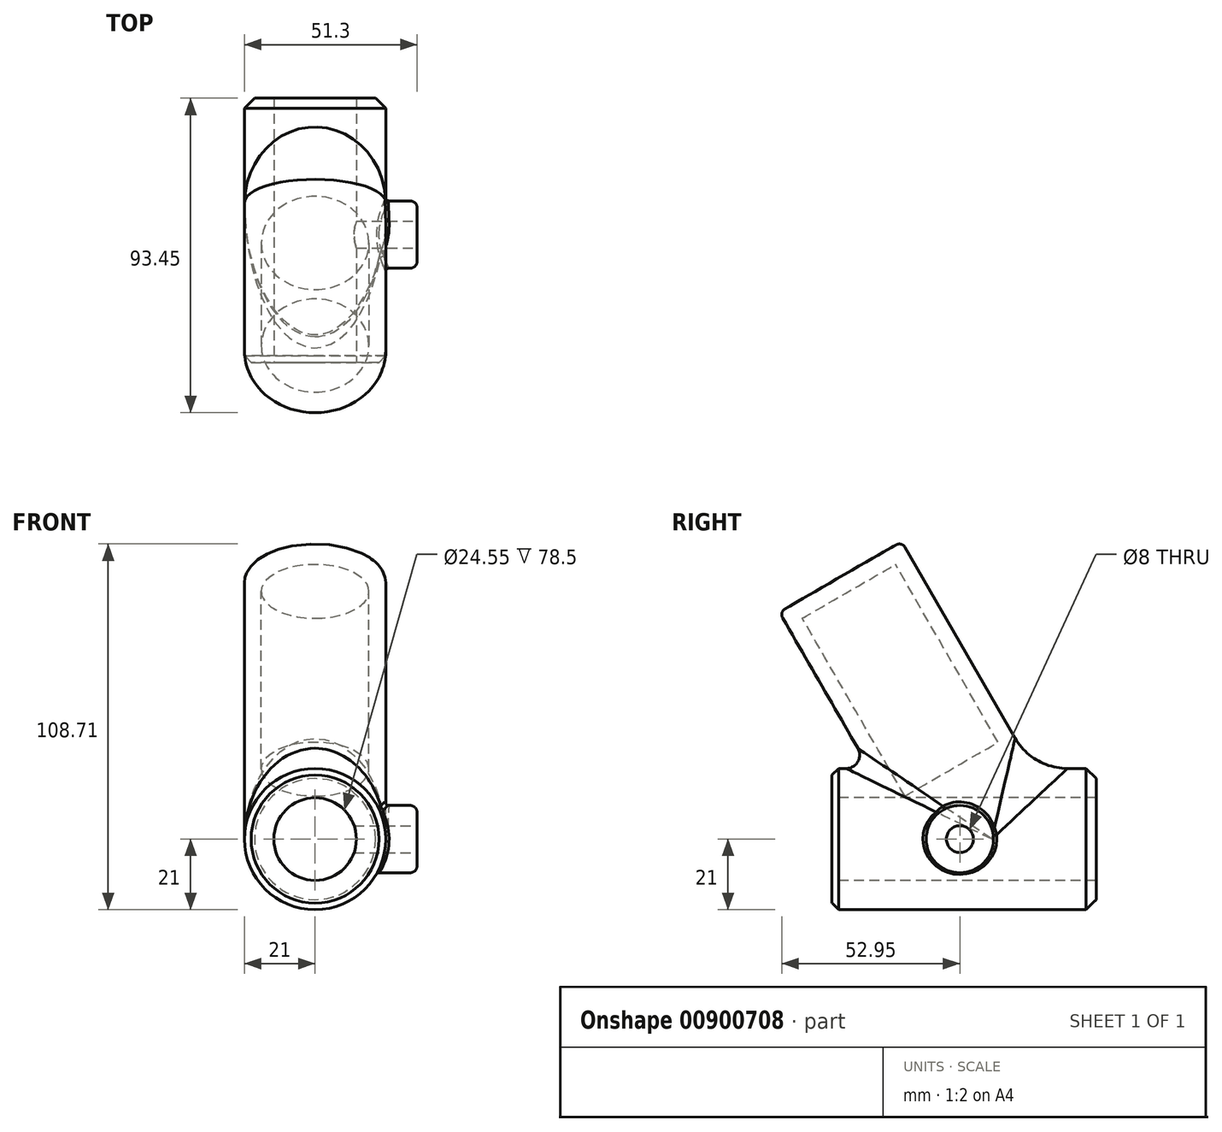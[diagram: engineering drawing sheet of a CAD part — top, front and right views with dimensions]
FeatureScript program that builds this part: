
annotation { "Feature Type Name" : "Feature", "Feature Type Description" : "" }
export const myFeature = defineFeature(function(context is Context, id is Id, definition is map)
    precondition{}
    {
        {
            var Q0;
            Q0=qCreatedBy(makeId("Front.planeOp"),FACE);
            var sketch = newSketch(context, id + "F0", { "sketchPlane" : qUnion([Q0])});
            skCircle(sketch, "E0", {"center": v(0, 0) * mm, "radius": 21 * mm});
            skSolve(sketch);
        }
        {
            var Q0;
            Q0=qSketchRegion(id+"F0",true);
            extrude(context, id + "F1", {"entities" : qUnion([Q0]), "oppositeDirection" : true, "depth" : 78.5 * mm, "offsetDistance" : 25 * mm});
        }
        {
            var Q0;
            Q0=qCreatedBy(makeId("Right.planeOp"),FACE);
            var sketch = newSketch(context, id + "F2", { "sketchPlane" : qUnion([Q0])});
            skLineSegment(sketch, "E1.0", {"start": v(29.31, -10.5) * mm, "end": v(-15.69, 67.44) * mm});
            skLineSegment(sketch, "E2", {"start": v(2.5, 77.94) * mm, "end": v(-15.69, 67.44) * mm});
            skLineSegment(sketch, "E3", {"start": v(47.5, 0) * mm, "end": v(29.31, -10.5) * mm});
            skLineSegment(sketch, "E4", {"start": v(2.5, 77.94) * mm, "end": v(47.5, 0) * mm});
            skSolve(sketch);
        }
        {
            var Q0;
            Q0=makeQuery(id+"F2.imprint","IMPRINT",FACE,{"disambiguationData":[TD([[makeQuery(id+"F2.imprint","IMPRINT",EDGE,{"derivedFrom":sQuery(id+"F2.wireOp",EDGE,"E1.0")}),-1.0]])]});
            var Q1;
            Q1=sQuery(id+"F2.wireOp",EDGE,"E4");
            revolve(context, id + "F3", {"operationType" : NewBodyOperationType.ADD, "surfaceOperationType" : NewSurfaceOperationType.NEW, "entities" : qUnion([Q0]), "axis" : qUnion([Q1]), "revolveType" : RevolveType.FULL});
        }
        {
            var Q0;
            Q0=makeQuery(id+"F3.boolean.opBoolean","INTERSECT",EDGE,{"disambiguationData":[OD(1.0)],"derivedFrom":[makeQuery(id+"F1.opExtrude","SWEPT_FACE",FACE,{"disambiguationData":[OSD([sQuery(id+"F0.wireOp",EDGE,"E0")])]}),makeQuery(id+"F3.opRevolve","SWEPT_FACE",FACE,{"disambiguationData":[OSD([sQuery(id+"F2.wireOp",EDGE,"E1.0")])]})]});
            fillet(context, id + "F4", {"entities" : qUnion([Q0]), "radius" : 18 * mm, "tangentPropagation" : true, "allowEdgeOverflow" : false});
        }
        {
            var Q0;
            Q0=makeQuery(id+"F3.boolean.opBoolean","INTERSECT",EDGE,{"disambiguationData":[OD(0.0)],"derivedFrom":[makeQuery(id+"F1.opExtrude","SWEPT_FACE",FACE,{"disambiguationData":[OSD([sQuery(id+"F0.wireOp",EDGE,"E0")])]}),makeQuery(id+"F3.opRevolve","SWEPT_FACE",FACE,{"disambiguationData":[OSD([sQuery(id+"F2.wireOp",EDGE,"E1.0")])]})]});
            fillet(context, id + "F5", {"entities" : qUnion([Q0]), "radius" : 4 * mm, "tangentPropagation" : true, "allowEdgeOverflow" : false});
        }
        {
            var Q0;
            Q0=makeQuery(id+"F1.opExtrude","CAP_FACE",FACE,{"disambiguationData":[OSD([sQuery(id+"F0.wireOp",EDGE,"E0")])],"isStart":true});
            var sketch = newSketch(context, id + "F6", { "sketchPlane" : qUnion([Q0])});
            skCircle(sketch, "E5", {"center": v(0, 0) * mm, "radius": 12.28 * mm});
            skSolve(sketch);
        }
        {
            var Q0;
            Q0=qSketchRegion(id+"F6",true);
            extrude(context, id + "F7", {"entities" : qUnion([Q0]), "operationType" : NewBodyOperationType.REMOVE, "oppositeDirection" : true, "depth" : 78.5 * mm, "offsetDistance" : 25 * mm});
        }
        {
            var Q0;
            Q0=makeQuery(id+"F1.opExtrude","CAP_EDGE",EDGE,{"disambiguationData":[OSD([sQuery(id+"F0.wireOp",EDGE,"E0")])],"isStart":false});
            chamfer(context, id + "F8", {"entities" : qUnion([Q0]), "width" : 3 * mm, "tangentPropagation" : true});
        }
        {
            var Q0;
            Q0=makeQuery(id+"F3.opRevolve","SWEPT_EDGE",EDGE,{"disambiguationData":[OSD([sQuery(id+"F2.wireOp",EDGE,"E1.0"),sQuery(id+"F2.wireOp",EDGE,"E2")])]});
            fillet(context, id + "F9", {"entities" : qUnion([Q0]), "radius" : 2 * mm, "tangentPropagation" : true, "allowEdgeOverflow" : false});
        }
        {
            var Q0;
            Q0=makeQuery(id+"F1.opExtrude","CAP_EDGE",EDGE,{"disambiguationData":[OSD([sQuery(id+"F0.wireOp",EDGE,"E0")])],"isStart":true});
            chamfer(context, id + "F10", {"entities" : qUnion([Q0]), "width" : 2 * mm, "tangentPropagation" : true});
        }
        {
            var Q0;
            Q0=qCreatedBy(makeId("Right.planeOp"),FACE);
            cPlane(context, id + "F11", {"entities" : qUnion([Q0]), "cplaneType" : CPlaneType.OFFSET, "offset" : 21 * mm, "width" : 150 * mm, "height" : 150 * mm});
        }
        {
            var Q0;
            Q0=qCreatedBy(id+"F11.planeOp",FACE);
            var sketch = newSketch(context, id + "F12", { "sketchPlane" : qUnion([Q0])});
            skCircle(sketch, "E6", {"center": v(38, 0) * mm, "radius": 10 * mm});
            skSolve(sketch);
        }
        {
            var Q0;
            Q0=qSketchRegion(id+"F12",true);
            extrude(context, id + "F13", {"entities" : qUnion([Q0]), "operationType" : NewBodyOperationType.ADD, "oppositeDirection" : true, "depth" : 3 * mm, "offsetDistance" : 25 * mm});
        }
        {
            var Q0;
            Q0=makeQuery(id+"F13.opExtrude","CAP_FACE",FACE,{"disambiguationData":[OSD([sQuery(id+"F12.wireOp",EDGE,"E6")])],"isStart":true});
            extrude(context, id + "F14", {"entities" : qUnion([Q0]), "operationType" : NewBodyOperationType.ADD, "depth" : 9.3 * mm, "offsetDistance" : 25 * mm});
        }
        {
            var Q0;
            Q0=makeQuery(id+"F14.opExtrude","CAP_EDGE",EDGE,{"disambiguationData":[OSD([sQuery(id+"F12.wireOp",EDGE,"E6")])],"isStart":false});
            fillet(context, id + "F15", {"entities" : qUnion([Q0]), "radius" : 2 * mm, "tangentPropagation" : true, "allowEdgeOverflow" : false});
        }
        {
            var Q0;
            Q0=makeQuery(id+"F14.opExtrude","CAP_FACE",FACE,{"disambiguationData":[OSD([sQuery(id+"F12.wireOp",EDGE,"E6")])],"isStart":false});
            var sketch = newSketch(context, id + "F16", { "sketchPlane" : qUnion([Q0])});
            skCircle(sketch, "E7", {"center": v(38, 0) * mm, "radius": 4 * mm});
            skSolve(sketch);
        }
        {
            var Q0;
            Q0=qSketchRegion(id+"F16",true);
            extrude(context, id + "F17", {"entities" : qUnion([Q0]), "operationType" : NewBodyOperationType.REMOVE, "oppositeDirection" : true, "depth" : 25 * mm, "offsetDistance" : 25 * mm});
        }
        {
            var Q0;
            {var subQ0=sQuery(id+"F12.wireOp",EDGE,"E6");var subQ1=makeQuery(id+"F13.opExtrude","SWEPT_FACE",FACE,{"disambiguationData":[OSD([subQ0])]});var subQ2=sQuery(id+"F2.wireOp",EDGE,"E1.0");var subQ3=sQuery(id+"F0.wireOp",EDGE,"E0");var subQ4=makeQuery(id+"F3.opRevolve","SWEPT_FACE",FACE,{"disambiguationData":[OSD([subQ2])]});var subQ5=makeQuery(id+"F1.opExtrude","SWEPT_FACE",FACE,{"disambiguationData":[OSD([subQ3])]});var subQ6=makeQuery(id+"F13.opExtrude","CAP_FACE",FACE,{"disambiguationData":[OSD([subQ0])],"isStart":true});Q0=makeQuery(id+"F14.boolean.opBoolean","MERGE",FACE,{"derivedFrom":[makeQuery(id+"F13.boolean.opBoolean","SPLIT",FACE,{"disambiguationData":[TD([subQ5,subQ1,subQ6])],"derivedFrom":subQ1}),makeQuery(id+"F13.boolean.opBoolean","SPLIT",FACE,{"disambiguationData":[TD([subQ5,subQ4,makeQuery(id+"F4.opFillet","BLEND_FACE",FACE,{"disambiguationData":[OSD([subQ3,subQ2])]}),subQ1,subQ6])],"derivedFrom":subQ1}),makeQuery(id+"F13.boolean.opBoolean","SPLIT",FACE,{"disambiguationData":[TD([subQ5,subQ4,makeQuery(id+"F5.opFillet","BLEND_FACE",FACE,{"disambiguationData":[OSD([subQ3,subQ2])]}),subQ1,subQ6])],"derivedFrom":subQ1}),makeQuery(id+"F14.opExtrude","SWEPT_FACE",FACE,{"disambiguationData":[OSD([subQ0])]})]});}
            var Q1;
            Q1=makeQuery(id+"F7.boolean.opBoolean","COPY",EDGE,{"derivedFrom":makeQuery(id+"F7.opExtrude","CAP_EDGE",EDGE,{"disambiguationData":[OSD([sQuery(id+"F6.wireOp",EDGE,"E5")])],"isStart":true})});
            var Q2;
            Q2=makeQuery(id+"F7.boolean.opBoolean","COPY",EDGE,{"derivedFrom":makeQuery(id+"F7.opExtrude","CAP_EDGE",EDGE,{"disambiguationData":[OSD([sQuery(id+"F6.wireOp",EDGE,"E5")])],"isStart":false})});
            var Q3;
            Q3=makeQuery(id+"F17.boolean.opBoolean","COPY",EDGE,{"derivedFrom":makeQuery(id+"F17.opExtrude","CAP_EDGE",EDGE,{"disambiguationData":[OSD([sQuery(id+"F16.wireOp",EDGE,"E7")])],"isStart":true})});
            fillet(context, id + "F18", {"entities" : qUnion([Q0, Q1, Q2, Q3]), "radius" : 1 * mm, "tangentPropagation" : true, "allowEdgeOverflow" : false});
        }
        {
            var Q0;
            Q0=makeQuery(id+"F3.opRevolve","SWEPT_FACE",FACE,{"disambiguationData":[OSD([sQuery(id+"F2.wireOp",EDGE,"E2")])]});
            cPlane(context, id + "F19", {"entities" : qUnion([Q0]), "cplaneType" : CPlaneType.OFFSET, "offset" : 5 * mm, "oppositeDirection" : true, "width" : 150 * mm, "height" : 150 * mm});
        }
        {
            var Q0;
            Q0=qCreatedBy(id+"F19.planeOp",FACE);
            var sketch = newSketch(context, id + "F20", { "sketchPlane" : qUnion([Q0])});
            skCircle(sketch, "E8", {"center": v(0, 41.14) * mm, "radius": 16 * mm});
            skSolve(sketch);
        }
        {
            var Q0;
            Q0 = qSketchRegion(id + "F20", true);
            extrude(context, id + "F21", {"entities" : qUnion([Q0]), "operationType" : NewBodyOperationType.REMOVE, "oppositeDirection" : true, "depth" : 61 * mm, "offsetDistance" : 25 * mm});
        }
    });
